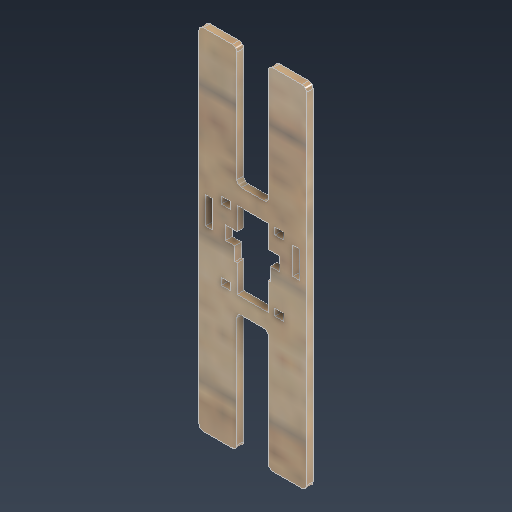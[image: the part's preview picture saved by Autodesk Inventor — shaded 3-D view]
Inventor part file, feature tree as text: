
AUTODESK INVENTOR PART (.ipt)
format: ipt  version: 2025.3 (Build 293356000, 356)  size: 262,144 bytes
history: native  units: mm
features: sketch x3, extrude x2, other x1
ambient origin geometry x8: Origin, YZ Plane, XZ Plane, XY Plane, X Axis, Y Axis, Z Axis, Center Point
bodies: Body1 (feature_tree)
feature tree (6):
  other  "實體1"
  extrude  "擠出1"  Depth=47.7mm
  sketch  "草圖3"
  extrude  "擠出4"  Depth=4.0mm
  sketch  "草圖1"
  sketch  "草圖5"
